# Revit family: RN 91040 Optifitt-Serra-Verschlusskappe
name_source: partatom
category: Rohrformteile
units: mm (PartAtom-declared; Revit-internal decimal feet)

## family parameters
Arbeitsebenenbasiert = Nein
Beim Laden mit Abzugskörper schneiden = Nein
Bemaßung runder Anschluss = Durchmesser verwenden
Gemeinsam genutzt = Nein
Immer vertikal = Ja
Teiletyp = Nicht definiert

## types (8) — shared parameters
1.010.00.2 Blattnummer der Richtlinie = 29
1.010.00.3 Ausgabedatum (Monat) der Richtlinie = 201308
1.010.00.4 Herstellername = R. Nussbaum AG
1.010.00.5 Revisionsdatum der Datei = 20190521
1.010.00.6 Webadresse des Herstellers = http://www.nussbaum.ch
1.100.00.4 Produktbezeichnung = Versorgung
1.110.00.2 Index = 3
1.110.00.4 Produktbezeichnung = Optifitt-Serra
1.960/3L.00.8 Link (URL) = https://www.nussbaum.ch
29.700.00.4 Produktname = Optifitt-Serra-Verschlusskappe
29.700.00.5 Produktkennung = 2
29.700.00.6 Querschnittsform = 1
29.700.00.7 Nennweitensystem = DN
29.700.00.8 Nenndrucksystem = PN
29.710.02.4 Nenndruck = 16
29.710.02.5 max. zul. Überdruck [hPa] = 1600
29.710.02.7 max. zul. Dauer-Betriebsdruck [hPa] = 1600
29.710.02.9 max. zul. Dauer-Betriebstemperatur [°C] = 90
Connector Visibility = Nein
EnclosingSpace Visibility = Nein
Hersteller = R. Nussbaum AG
URL = https://www.nussbaum.ch

## per-type parameters (varying)
| type | 1.800.00.3 TGA-Nummer | 1.800.00.4 Kommentarfeld | 1.810.00.3 Hersteller-Bestellnummer | 1.810.00.4 DATANORM-Nummer | 1.810.00.5 StLB-Nummer | 1.810.00.6 GTIN-Nummer | 29.710.02.10 Formstück-Gewicht [kg] | 29.710.02.3 Benennung | CONNECTOR0_DIAMETER_dX_0r | CONNECTOR0_dX_01 | CONNECTOR0_ref_dX | Modell | R. Nussbaum AG 91040.52 de Visibility | R. Nussbaum AG 91040.53 de Visibility | R. Nussbaum AG 91040.54 de Visibility | R. Nussbaum AG 91040.55 de Visibility | R. Nussbaum AG 91040.56 de Visibility | R. Nussbaum AG 91040.57 de Visibility | R. Nussbaum AG 91040.58 de Visibility | R. Nussbaum AG 91040.59 de Visibility | Typenkommentare |
| DN=50 | 01900300000000000000000000000000000000000000000023000000000000000022 | 91040.59, Optifitt-Serra-Verschlusskappe, DN=50, L=21 | 91040.59 | 91040.59 | 216.137 | 7612945036223 | 0.256 | Optifitt-Serra-Verschlusskappe, DN=50, L=21 | 50 mm | 17 mm | 17 mm | 91040.59 | Nein | Nein | Nein | Nein | Nein | Nein | Nein | Ja | Optifitt-Serra-Verschlusskappe  DN=50 |
| DN=40 | 01900300000000000000000000000000000000000000000023000000000000000021 | 91040.58, Optifitt-Serra-Verschlusskappe, DN=40, L=13 | 91040.58 | 91040.58 | 216.136 | 7612945036216 | 0.137 | Optifitt-Serra-Verschlusskappe, DN=40, L=13 | 40 mm | 11 mm | 11 mm | 91040.58 | Nein | Nein | Nein | Nein | Nein | Nein | Ja | Nein | Optifitt-Serra-Verschlusskappe  DN=40 |
| DN=32 | 01900300000000000000000000000000000000000000000023000000000000000020 | 91040.57, Optifitt-Serra-Verschlusskappe, DN=32, L=14 | 91040.57 | 91040.57 | 216.135 | 7612945036209 | 0.071 | Optifitt-Serra-Verschlusskappe, DN=32, L=14 | 32 mm | 12 mm  [stored 0.0393701 ft] | 12 mm  [stored 0.0393701 ft] | 91040.57 | Nein | Nein | Nein | Nein | Nein | Ja | Nein | Nein | Optifitt-Serra-Verschlusskappe  DN=32 |
| DN=25 | 01900300000000000000000000000000000000000000000023000000000000000019 | 91040.56, Optifitt-Serra-Verschlusskappe, DN=25, L=16 | 91040.56 | 91040.56 | 216.134 | 7612945036193 | 0.06 | Optifitt-Serra-Verschlusskappe, DN=25, L=16 | 25 mm  [stored 0.082021 ft] | 13 mm | 13 mm | 91040.56 | Nein | Nein | Nein | Nein | Ja | Nein | Nein | Nein | Optifitt-Serra-Verschlusskappe  DN=25 |
| DN=20 | 01900300000000000000000000000000000000000000000023000000000000000018 | 91040.55, Optifitt-Serra-Verschlusskappe, DN=20, L=15 | 91040.55 | 91040.55 | 216.133 | 7612945036186 | 0.048 | Optifitt-Serra-Verschlusskappe, DN=20, L=15 | 20 mm | 12 mm  [stored 0.0393701 ft] | 12 mm  [stored 0.0393701 ft] | 91040.55 | Nein | Nein | Nein | Ja | Nein | Nein | Nein | Nein | Optifitt-Serra-Verschlusskappe  DN=20 |
| DN=15 | 01900300000000000000000000000000000000000000000023000000000000000017 | 91040.54, Optifitt-Serra-Verschlusskappe, DN=15, L=12 | 91040.54 | 91040.54 | 216.132 | 7612945036179 | 0.018 | Optifitt-Serra-Verschlusskappe, DN=15, L=12 | 15 mm | 10 mm  [stored 0.0328084 ft] | 10 mm  [stored 0.0328084 ft] | 91040.54 | Nein | Nein | Ja | Nein | Nein | Nein | Nein | Nein | Optifitt-Serra-Verschlusskappe  DN=15 |
| DN=10 | 01900300000000000000000000000000000000000000000023000000000000000016 | 91040.53, Optifitt-Serra-Verschlusskappe, DN=10, L=10 | 91040.53 | 91040.53 | 216.131 | 7612945036162 | 0.012 | Optifitt-Serra-Verschlusskappe, DN=10, L=10 | 12 mm  [stored 0.0393701 ft] | 8 mm  [stored 0.0262467 ft] | 8 mm  [stored 0.0262467 ft] | 91040.53 | Nein | Ja | Nein | Nein | Nein | Nein | Nein | Nein | Optifitt-Serra-Verschlusskappe  DN=10 |
| DN=1 | 01900300000000000000000000000000000000000000000023000000000000000015 | 91040.52, Optifitt-Serra-Verschlusskappe, DN=10, L=10 | 91040.52 | 91040.52 |  | 7612945036155 | 0.009 | Optifitt-Serra-Verschlusskappe, DN=10, L=10 | 10 mm  [stored 0.0328084 ft] | 8 mm  [stored 0.0262467 ft] | 8 mm  [stored 0.0262467 ft] | 91040.52 | Ja | Nein | Nein | Nein | Nein | Nein | Nein | Nein | Optifitt-Serra-Verschlusskappe  DN=10 |

note: [stored X ft] marks values corroborated as IEEE doubles in the binary element streams (Revit-internal decimal feet)

## geometry (parser evidence)
native form markers: Sweep x2
no freeform markers — native parametric forms only
